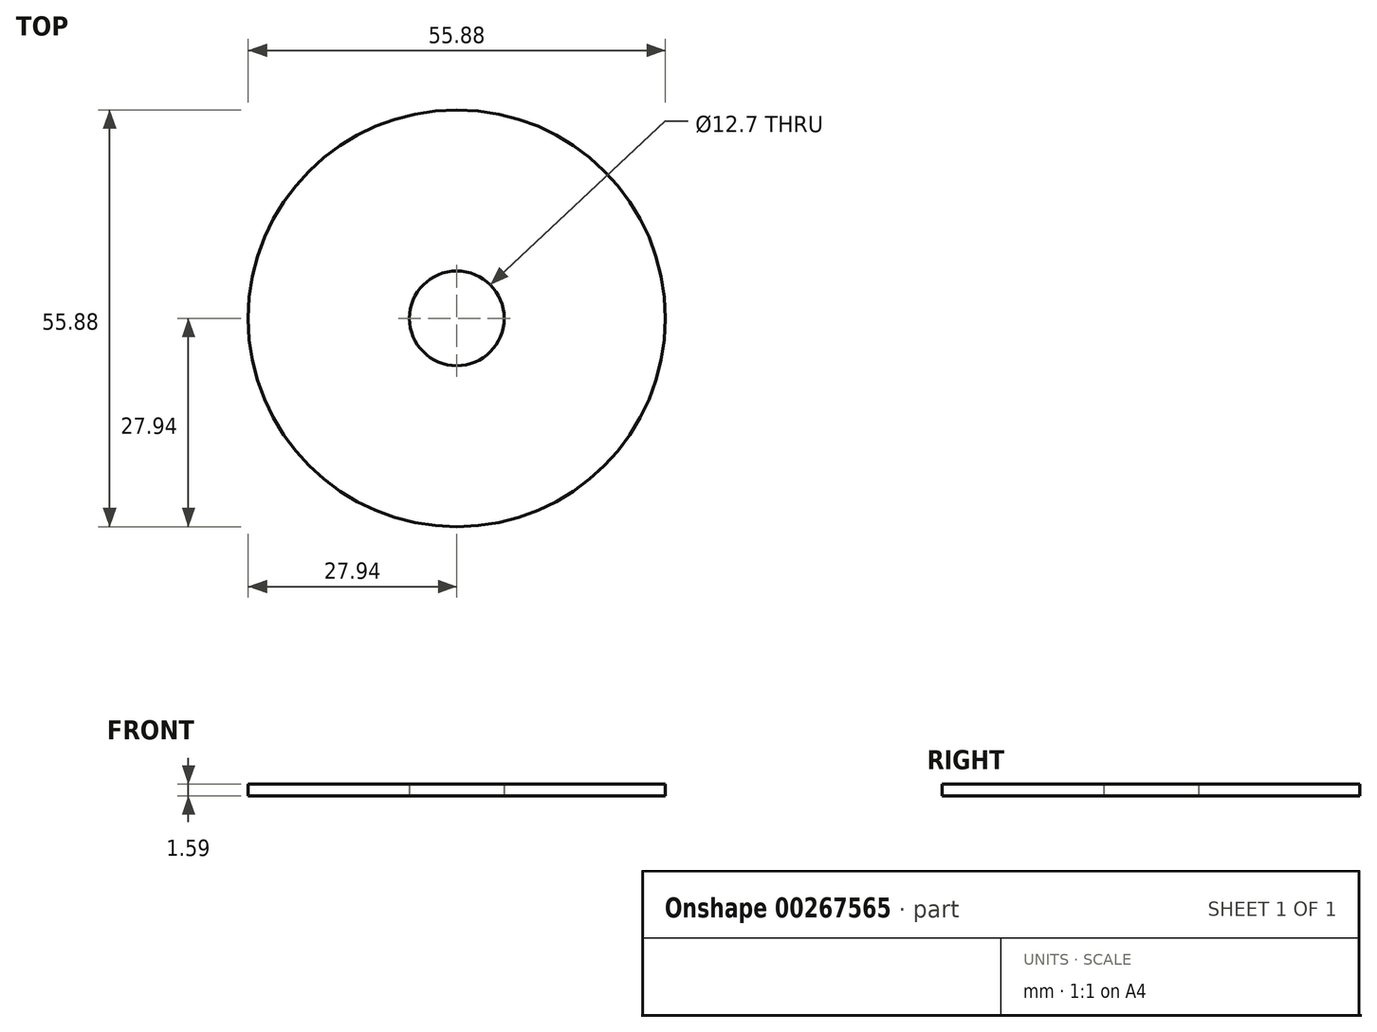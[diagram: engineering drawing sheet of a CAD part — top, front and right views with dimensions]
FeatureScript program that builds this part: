
annotation { "Feature Type Name" : "Feature", "Feature Type Description" : "" }
export const myFeature = defineFeature(function(context is Context, id is Id, definition is map)
    precondition{}
    {
        {
            var Q0;
            Q0=qCreatedBy(makeId("Top.planeOp"),FACE);
            var sketch = newSketch(context, id + "F0", { "sketchPlane" : qUnion([Q0])});
            skCircle(sketch, "E0", {"center": v(0, 0) * mm, "radius": 27.94 * mm});
            skCircle(sketch, "E1", {"center": v(0, 0) * mm, "radius": 6.35 * mm});
            skSolve(sketch);
        }
        {
            var Q0;
            Q0=makeQuery(id+"F0.imprint","IMPRINT",FACE,{"disambiguationData":[TD([[makeQuery(id+"F0.imprint","IMPRINT",EDGE,{"derivedFrom":sQuery(id+"F0.wireOp",EDGE,"E0")}),1.0]])]});
            extrude(context, id + "F1", {"entities" : qUnion([Q0]), "depth" : 1.59 * mm});
        }
    });
